# Revit family: Zahnplatte M 6
name_source: partatom
category: HLS-Bauteile
revit_build: Autodesk Revit 2017 (Build: 20190507_1515(x64)
units: mm (PartAtom-declared; Revit-internal decimal feet)

## family parameters
Arbeitsebenenbasiert = Ja
Beim Laden mit Abzugskörper schneiden = Nein
Bemaßung runder Anschluss = Durchmesser verwenden
Gemeinsam genutzt = Ja
Immer vertikal = Nein
Raumberechnungspunkt = Nein
Teiletyp = Normal

## types (1)
- MEFA Zahnplatte M 6
    Abmessung = 34 x 21 x 12 mm
    Anzugsmoment = 0.00 kN-m
    Artikelnummer = 0818000
    Breite = 21 mm  [stored 0.0688976 ft]
    EAN = 4250928420541
    Fabrikat = MEFA
    Firma = MEFA Befestigungs- und Montagesysteme GmbH
    Form = einschwenkbar
    Gewicht = 0.05 kg
    Gewicht pro Bauteil = 0.05 kg
    Gewinde = M6
    Kurztext1 = Zahnplatte
    Kurztext2 = M6 34 x 21 mm gvz
    Länge = 34 mm
    Material = Stahl
    Mengeneinheit = St
    Oberflaeche = galvanisch verzinkt
    Profil = C-Profil
    Profiltyp = 45
    Schienenbreite = 45 mm
    Stärke Material = 12 mm  [stored 0.0393701 ft]
    Vorgabe-Ansicht = 1219 mm
    d2 = 3 mm  [stored 0.00984252 ft]
    vpe = 100 St

note: [stored X ft] marks values corroborated as IEEE doubles in the binary element streams (Revit-internal decimal feet)
